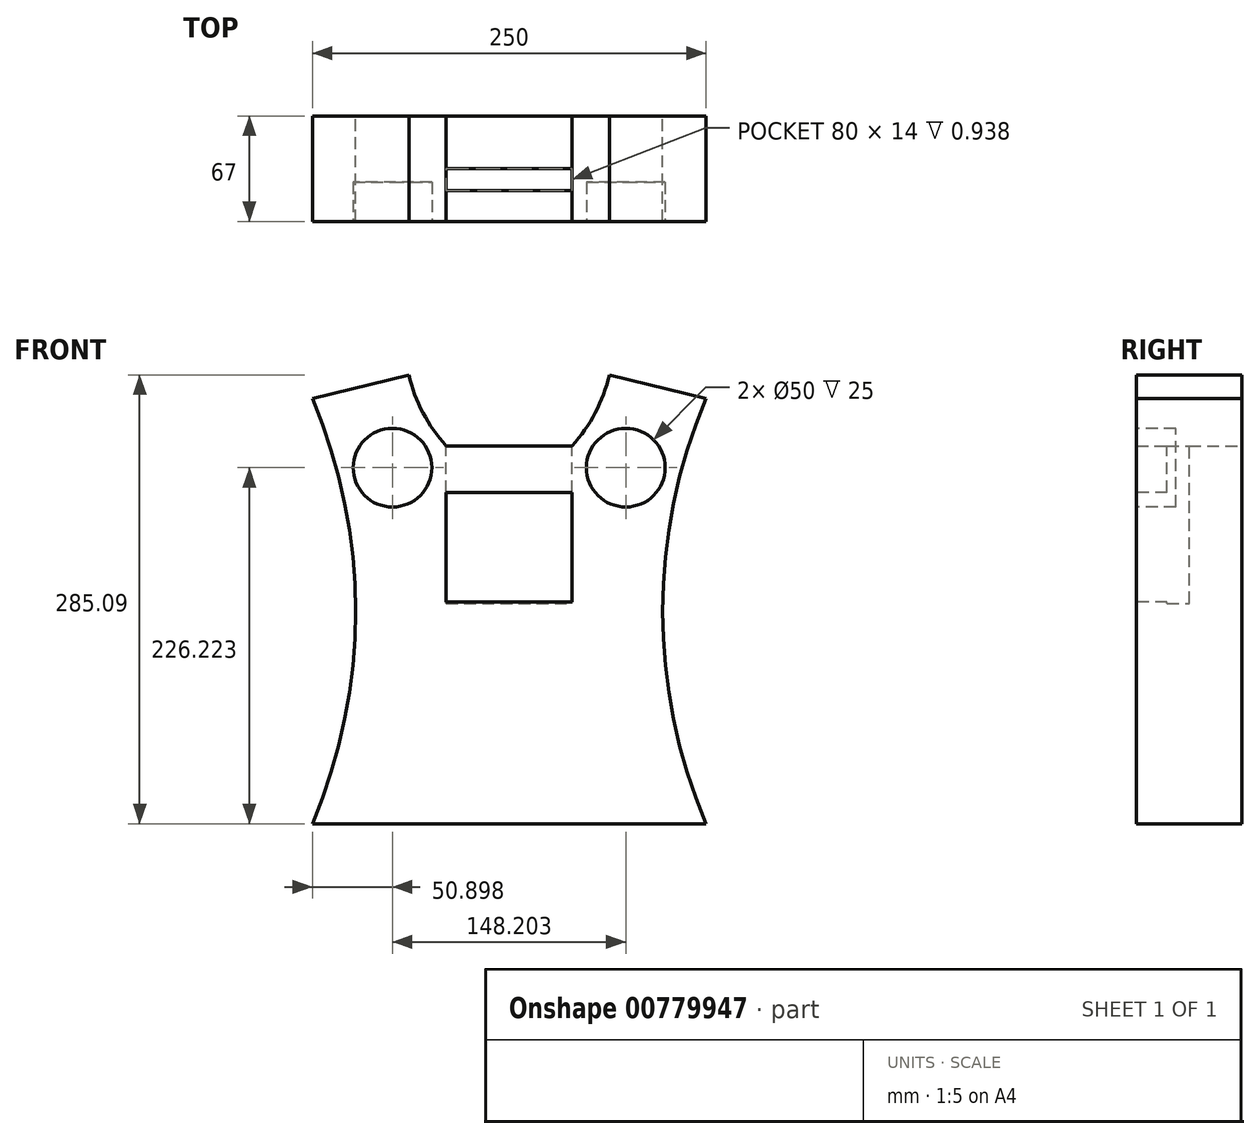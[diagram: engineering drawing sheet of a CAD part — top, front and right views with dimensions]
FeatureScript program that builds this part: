
annotation { "Feature Type Name" : "Feature", "Feature Type Description" : "" }
export const myFeature = defineFeature(function(context is Context, id is Id, definition is map)
    precondition{}
    {
        {
            var Q0;
            Q0=qCreatedBy(makeId("Front.planeOp"),FACE);
            var sketch = newSketch(context, id + "F0", { "sketchPlane" : qUnion([Q0])});
            skLineSegment(sketch, "E0.bottom", {"start": v(0, 0) * mm, "end": v(125, 0) * mm});
            skArc(sketch, "E1", {"start": v(0, 0) * mm, "mid": v(27.48, 135) * mm, "end": v(0, 270) * mm});
            skLineSegment(sketch, "E2", {"start": v(125, 0) * mm, "end": v(125, 240) * mm});
            skPoint(sketch, "E0.right.end.orphan", {"position": v(250, 270) * mm});
            skPoint(sketch, "E3.orphan", {"position": v(250, 0) * mm});
            skLineSegment(sketch, "E4", {"start": v(125, 240) * mm, "end": v(85, 240) * mm});
            skArc(sketch, "E5", {"start": v(61.28, 285.1) * mm, "mid": v(70.31, 261.06) * mm, "end": v(85, 240) * mm});
            skLineSegment(sketch, "E6", {"start": v(0, 270) * mm, "end": v(61.28, 285.1) * mm});
            skPoint(sketch, "E7.orphan", {"position": v(125, 270) * mm});
            skLineSegment(sketch, "E8.MirrorCS", {"start": v(125, 240) * mm, "end": v(165, 240) * mm});
            skArc(sketch, "E9.MirrorCS", {"start": v(188.72, 285.1) * mm, "mid": v(179.69, 261.06) * mm, "end": v(165, 240) * mm});
            skLineSegment(sketch, "E10.MirrorCS", {"start": v(250, 270) * mm, "end": v(188.72, 285.1) * mm});
            skArc(sketch, "E11.MirrorCS", {"start": v(250, 0) * mm, "mid": v(222.52, 135) * mm, "end": v(250, 270) * mm});
            skLineSegment(sketch, "E12.MirrorCS", {"start": v(250, 0) * mm, "end": v(125, 0) * mm});
            skSolve(sketch);
        }
        {
            var Q0;
            Q0=makeQuery(id+"F0.imprint","IMPRINT",FACE,{"disambiguationData":[TD([[makeQuery(id+"F0.imprint","IMPRINT",EDGE,{"derivedFrom":sQuery(id+"F0.wireOp",EDGE,"E0.bottom")}),1.0]])]});
            var Q1;
            Q1=makeQuery(id+"F0.imprint","IMPRINT",FACE,{"disambiguationData":[TD([[makeQuery(id+"F0.imprint","IMPRINT",EDGE,{"derivedFrom":sQuery(id+"F0.wireOp",EDGE,"E2")}),-1.0]])]});
            extrude(context, id + "F1", {"entities" : qUnion([Q0, Q1]), "depth" : 67 * mm, "offsetDistance" : 25 * mm});
        }
        {
            var Q0;
            Q0=makeQuery(id+"F1.opExtrude","CAP_FACE",FACE,{"disambiguationData":[OSD([sQuery(id+"F0.wireOp",EDGE,"E0.bottom"),sQuery(id+"F0.wireOp",EDGE,"E1"),sQuery(id+"F0.wireOp",EDGE,"E4"),sQuery(id+"F0.wireOp",EDGE,"E5"),sQuery(id+"F0.wireOp",EDGE,"E6"),sQuery(id+"F0.wireOp",EDGE,"E8.MirrorCS"),sQuery(id+"F0.wireOp",EDGE,"E9.MirrorCS"),sQuery(id+"F0.wireOp",EDGE,"E10.MirrorCS"),sQuery(id+"F0.wireOp",EDGE,"E11.MirrorCS"),sQuery(id+"F0.wireOp",EDGE,"E12.MirrorCS")])],"isStart":false});
            var sketch = newSketch(context, id + "F2", { "sketchPlane" : qUnion([Q0])});
            skLineSegment(sketch, "E13.bottom", {"start": v(85, 210.59) * mm, "end": v(165, 210.59) * mm});
            skLineSegment(sketch, "E13.top", {"start": v(85, 140.94) * mm, "end": v(165, 140.94) * mm});
            skLineSegment(sketch, "E13.left", {"start": v(85, 210.59) * mm, "end": v(85, 140.94) * mm});
            skLineSegment(sketch, "E13.right", {"start": v(165, 210.59) * mm, "end": v(165, 140.94) * mm});
            skLineSegment(sketch, "E14", {"start": v(125, 240) * mm, "end": v(125, 44.28) * mm});
            skCircle(sketch, "E15", {"center": v(50.9, 226.22) * mm, "radius": 25 * mm});
            skCircle(sketch, "E16.MirrorC", {"center": v(199.1, 226.22) * mm, "radius": 25 * mm});
            skSolve(sketch);
        }
        {
            var Q0;
            {var subQ0=sQuery(id+"F2.wireOp",EDGE,"E13.left");Q0=makeQuery(id+"F2.imprint","IMPRINT",FACE,{"disambiguationData":[TD([[makeQuery(id+"F2.imprint","IMPRINT",EDGE,{"derivedFrom":subQ0}),1.0]])]});}
            var Q1;
            {var subQ0=sQuery(id+"F2.wireOp",EDGE,"E13.right");Q1=makeQuery(id+"F2.imprint","IMPRINT",FACE,{"disambiguationData":[TD([[makeQuery(id+"F2.imprint","IMPRINT",EDGE,{"derivedFrom":subQ0}),-1.0]])]});}
            extrude(context, id + "F3", {"entities" : qUnion([Q0, Q1]), "operationType" : NewBodyOperationType.REMOVE, "oppositeDirection" : true, "depth" : 28 * mm, "offsetDistance" : 25 * mm});
        }
        {
            var Q0;
            Q0 = qSketchRegion(id + "F2", true);
            extrude(context, id + "F4", {"entities" : qUnion([Q0]), "operationType" : NewBodyOperationType.REMOVE, "oppositeDirection" : true, "depth" : 25 * mm, "offsetDistance" : 25 * mm});
        }
        {
            var Q0;
            Q0=makeQuery(id+"F1.opExtrude","SWEPT_FACE",FACE,{"disambiguationData":[OSD([sQuery(id+"F0.wireOp",EDGE,"E4"),sQuery(id+"F0.wireOp",EDGE,"E8.MirrorCS")])]});
            var sketch = newSketch(context, id + "F5", { "sketchPlane" : qUnion([Q0])});
            skLineSegment(sketch, "E17.bottom", {"start": v(85, -33.5) * mm, "end": v(165, -33.5) * mm});
            skLineSegment(sketch, "E17.top", {"start": v(85, -47.5) * mm, "end": v(165, -47.5) * mm});
            skLineSegment(sketch, "E17.left", {"start": v(85, -33.5) * mm, "end": v(85, -47.5) * mm});
            skLineSegment(sketch, "E17.right", {"start": v(165, -33.5) * mm, "end": v(165, -47.5) * mm});
            skSolve(sketch);
        }
        {
            var Q0;
            Q0=makeQuery(id+"F5.imprint","IMPRINT",FACE,{"disambiguationData":[TD([[makeQuery(id+"F5.imprint","IMPRINT",EDGE,{"derivedFrom":sQuery(id+"F5.wireOp",EDGE,"E17.bottom")}),-1.0]])]});
            extrude(context, id + "F6", {"entities" : qUnion([Q0]), "operationType" : NewBodyOperationType.REMOVE, "oppositeDirection" : true, "depth" : 100 * mm, "offsetDistance" : 25 * mm});
        }
    });
